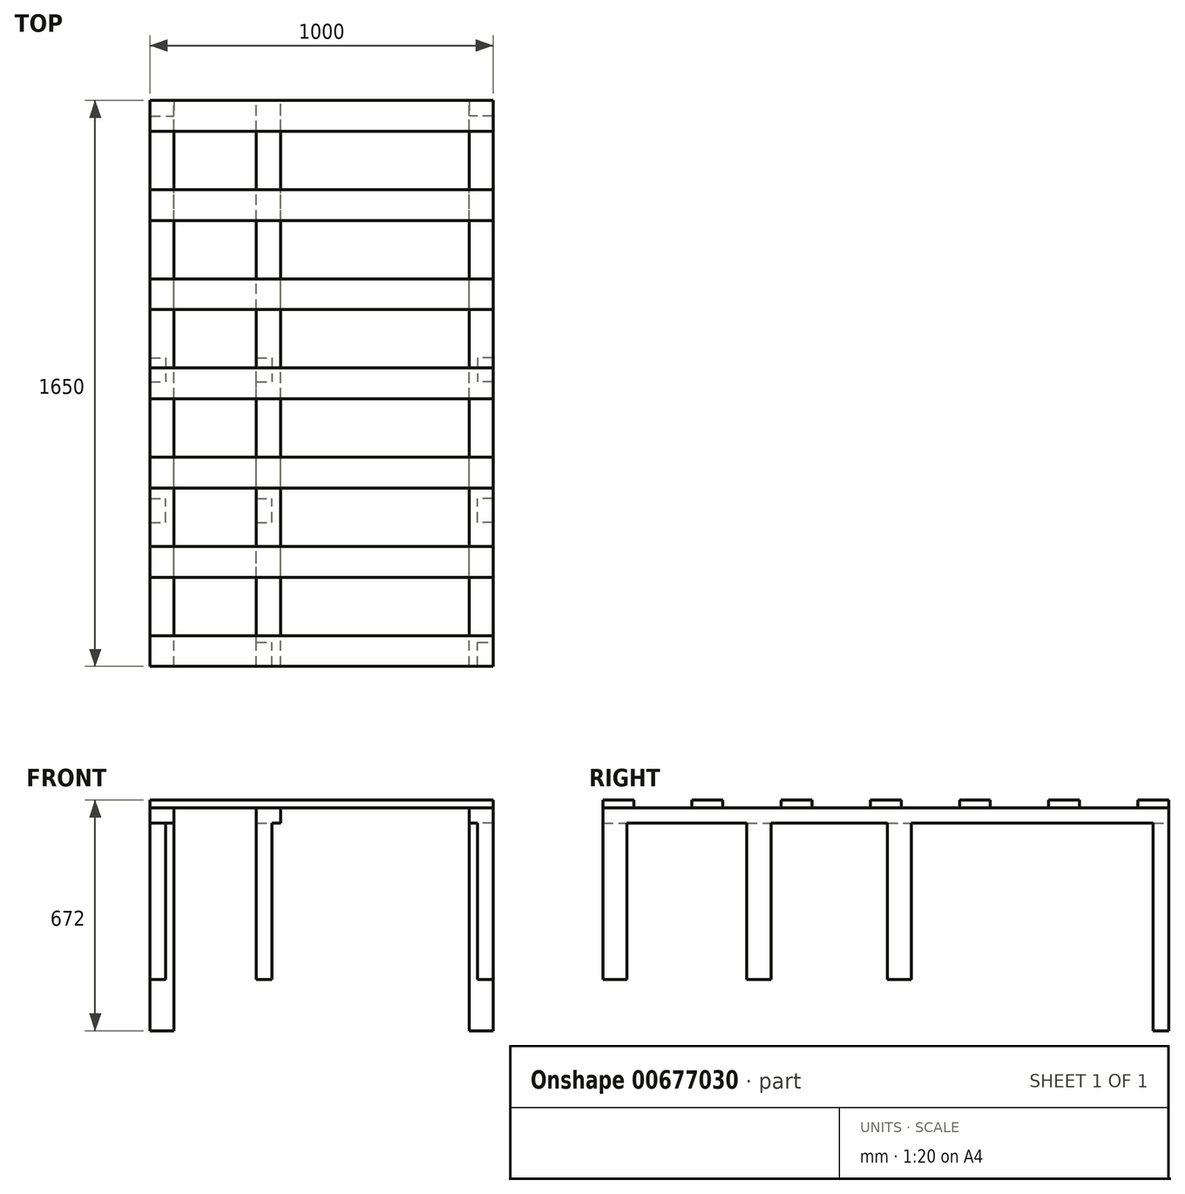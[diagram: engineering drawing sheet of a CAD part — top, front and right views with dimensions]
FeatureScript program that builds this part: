
annotation { "Feature Type Name" : "Feature", "Feature Type Description" : "" }
export const myFeature = defineFeature(function(context is Context, id is Id, definition is map)
    precondition{}
    {
        {
            var Q0;
            Q0=qCreatedBy(makeId("Top.planeOp"),FACE);
            var sketch = newSketch(context, id + "F0", { "sketchPlane" : qUnion([Q0])});
            skLineSegment(sketch, "E0.MirrorCS", {"start": v(-35, -1650) * mm, "end": v(35, -1650) * mm});
            skLineSegment(sketch, "E1.MirrorCS", {"start": v(-35, 0) * mm, "end": v(35, 0) * mm});
            skLineSegment(sketch, "E2.MirrorCS", {"start": v(655, 0) * mm, "end": v(585, 0) * mm});
            skLineSegment(sketch, "E3.MirrorCS", {"start": v(-345, 0) * mm, "end": v(-275, 0) * mm});
            skLineSegment(sketch, "E4.MirrorCS", {"start": v(-275, -1650) * mm, "end": v(-275, 0) * mm});
            skLineSegment(sketch, "E5.MirrorCS", {"start": v(585, -1650) * mm, "end": v(585, 0) * mm});
            skLineSegment(sketch, "E6.MirrorCS", {"start": v(35, -1650) * mm, "end": v(35, 0) * mm});
            skLineSegment(sketch, "E7.MirrorCS", {"start": v(655, -1650) * mm, "end": v(655, 0) * mm});
            skLineSegment(sketch, "E8.MirrorCS", {"start": v(-345, -1650) * mm, "end": v(-345, 0) * mm});
            skLineSegment(sketch, "E9.MirrorCS", {"start": v(-35, -1650) * mm, "end": v(-35, 0) * mm});
            skLineSegment(sketch, "E10.MirrorCS", {"start": v(0, -2563.12) * mm, "end": v(0, 0) * mm, "construction": true});
            skLineSegment(sketch, "E11", {"start": v(655, -1650) * mm, "end": v(585, -1650) * mm});
            skLineSegment(sketch, "E12", {"start": v(-275, -1650) * mm, "end": v(-345, -1650) * mm});
            skLineSegment(sketch, "E13", {"start": v(585, 0) * mm, "end": v(-345, 0) * mm, "construction": true});
            skLineSegment(sketch, "E14", {"start": v(585, -1650) * mm, "end": v(-275, -1650) * mm, "construction": true});
            skSolve(sketch);
        }
        {
            var Q0;
            Q0 = qSketchRegion(id + "F0", true);
            var Q1;
            {var subQ0=sQuery(id+"F0.wireOp",EDGE,"24e93d22-9b63-4a5b-b6a3-05b6ad89516c20.MirrorCS");var subQ1=sQuery(id+"F0.wireOp",EDGE,"E6.MirrorCS");var subQ2=makeQuery(id+"F0.imprint","INTERSECT",VERTEX,{"derivedFrom":[subQ1,subQ0]});Q1=makeQuery(id+"F0.imprint","IMPRINT",FACE,{"disambiguationData":[TD([[makeQuery(id+"F0.imprint","IMPRINT",EDGE,{"disambiguationData":[TD([[subQ2,-1.0]])],"derivedFrom":subQ1}),1.0]])]});}
            extrude(context, id + "F1", {"entities" : qUnion([Q0, Q1]), "depth" : 45 * mm, "offsetDistance" : 25 * mm});
        }
        {
            var Q0;
            Q0=makeQuery(id+"F1.opExtrude","CAP_FACE",FACE,{"disambiguationData":[OSD([sQuery(id+"F0.wireOp",EDGE,"E1.MirrorCS"),sQuery(id+"F0.wireOp",EDGE,"E2.MirrorCS"),sQuery(id+"F0.wireOp",EDGE,"E3.MirrorCS"),sQuery(id+"F0.wireOp",EDGE,"E4.MirrorCS"),sQuery(id+"F0.wireOp",EDGE,"E5.MirrorCS"),sQuery(id+"F0.wireOp",EDGE,"E6.MirrorCS"),sQuery(id+"F0.wireOp",EDGE,"24e93d22-9b63-4a5b-b6a3-05b6ad89516c14.MirrorCS"),sQuery(id+"F0.wireOp",EDGE,"E7.MirrorCS"),sQuery(id+"F0.wireOp",EDGE,"E8.MirrorCS"),sQuery(id+"F0.wireOp",EDGE,"E9.MirrorCS"),sQuery(id+"F0.wireOp",EDGE,"24e93d22-9b63-4a5b-b6a3-05b6ad89516c20.MirrorCS")])],"isStart":true});
            var sketch = newSketch(context, id + "F2", { "sketchPlane" : qUnion([Q0])});
            skLineSegment(sketch, "E15.bottom", {"start": v(610, 1650) * mm, "end": v(655, 1650) * mm});
            skLineSegment(sketch, "E15.top", {"start": v(610, 1580) * mm, "end": v(655, 1580) * mm});
            skLineSegment(sketch, "E15.left", {"start": v(610, 1650) * mm, "end": v(610, 1580) * mm});
            skLineSegment(sketch, "E15.right", {"start": v(655, 1650) * mm, "end": v(655, 1580) * mm});
            skLineSegment(sketch, "E16", {"start": v(-766.64, 750) * mm, "end": v(804.53, 750) * mm, "construction": true});
            skLineSegment(sketch, "E17.bottom", {"start": v(-345, 750) * mm, "end": v(-300, 750) * mm});
            skLineSegment(sketch, "E17.top", {"start": v(-345, 820) * mm, "end": v(-300, 820) * mm});
            skLineSegment(sketch, "E17.left", {"start": v(-345, 750) * mm, "end": v(-345, 820) * mm});
            skLineSegment(sketch, "E17.right", {"start": v(-300, 750) * mm, "end": v(-300, 820) * mm});
            skLineSegment(sketch, "E18.bottom", {"start": v(655, 750) * mm, "end": v(610, 750) * mm});
            skLineSegment(sketch, "E18.top", {"start": v(655, 820) * mm, "end": v(610, 820) * mm});
            skLineSegment(sketch, "E18.left", {"start": v(655, 750) * mm, "end": v(655, 820) * mm});
            skLineSegment(sketch, "E18.right", {"start": v(610, 750) * mm, "end": v(610, 820) * mm});
            skLineSegment(sketch, "E19.bottom", {"start": v(-345, 0) * mm, "end": v(-275, 0) * mm});
            skLineSegment(sketch, "E19.top", {"start": v(-345, 45) * mm, "end": v(-275, 45) * mm});
            skLineSegment(sketch, "E19.left", {"start": v(-345, 0) * mm, "end": v(-345, 45) * mm});
            skLineSegment(sketch, "E19.right", {"start": v(-275, 0) * mm, "end": v(-275, 45) * mm});
            skLineSegment(sketch, "E20.bottom", {"start": v(655, 0) * mm, "end": v(585, 0) * mm});
            skLineSegment(sketch, "E20.top", {"start": v(655, 45) * mm, "end": v(585, 45) * mm});
            skLineSegment(sketch, "E20.left", {"start": v(655, 0) * mm, "end": v(655, 45) * mm});
            skLineSegment(sketch, "E20.right", {"start": v(585, 0) * mm, "end": v(585, 45) * mm});
            skLineSegment(sketch, "E21.bottom", {"start": v(-35, 750) * mm, "end": v(10, 750) * mm});
            skLineSegment(sketch, "E21.top", {"start": v(-35, 820) * mm, "end": v(10, 820) * mm});
            skLineSegment(sketch, "E21.left", {"start": v(-35, 750) * mm, "end": v(-35, 820) * mm});
            skLineSegment(sketch, "E21.right", {"start": v(10, 750) * mm, "end": v(10, 820) * mm});
            skLineSegment(sketch, "E22.bottom", {"start": v(-345, 1650) * mm, "end": v(-300, 1650) * mm});
            skLineSegment(sketch, "E22.top", {"start": v(-345, 1580) * mm, "end": v(-300, 1580) * mm});
            skLineSegment(sketch, "E22.left", {"start": v(-345, 1650) * mm, "end": v(-345, 1580) * mm});
            skLineSegment(sketch, "E22.right", {"start": v(-300, 1650) * mm, "end": v(-300, 1580) * mm});
            skLineSegment(sketch, "E23.bottom", {"start": v(-35, 1650) * mm, "end": v(10, 1650) * mm});
            skLineSegment(sketch, "E23.top", {"start": v(-35, 1580) * mm, "end": v(10, 1580) * mm});
            skLineSegment(sketch, "E23.left", {"start": v(-35, 1650) * mm, "end": v(-35, 1580) * mm});
            skLineSegment(sketch, "E23.right", {"start": v(10, 1650) * mm, "end": v(10, 1580) * mm});
            skLineSegment(sketch, "E24.bottom", {"start": v(-345, 1230) * mm, "end": v(-300, 1230) * mm});
            skLineSegment(sketch, "E24.top", {"start": v(-345, 1160) * mm, "end": v(-300, 1160) * mm});
            skLineSegment(sketch, "E24.left", {"start": v(-345, 1230) * mm, "end": v(-345, 1160) * mm});
            skLineSegment(sketch, "E24.right", {"start": v(-300, 1230) * mm, "end": v(-300, 1160) * mm});
            skLineSegment(sketch, "E25.bottom", {"start": v(-35, 1230) * mm, "end": v(10, 1230) * mm});
            skLineSegment(sketch, "E25.top", {"start": v(-35, 1160) * mm, "end": v(10, 1160) * mm});
            skLineSegment(sketch, "E25.left", {"start": v(-35, 1230) * mm, "end": v(-35, 1160) * mm});
            skLineSegment(sketch, "E25.right", {"start": v(10, 1230) * mm, "end": v(10, 1160) * mm});
            skLineSegment(sketch, "E26.bottom", {"start": v(655, 1230) * mm, "end": v(610, 1230) * mm});
            skLineSegment(sketch, "E26.top", {"start": v(655, 1160) * mm, "end": v(610, 1160) * mm});
            skLineSegment(sketch, "E26.left", {"start": v(655, 1230) * mm, "end": v(655, 1160) * mm});
            skLineSegment(sketch, "E26.right", {"start": v(610, 1230) * mm, "end": v(610, 1160) * mm});
            skSolve(sketch);
        }
        {
            var Q0;
            Q0=makeQuery(id+"F2.imprint","IMPRINT",FACE,{"disambiguationData":[TD([[makeQuery(id+"F2.imprint","IMPRINT",EDGE,{"derivedFrom":sQuery(id+"F2.wireOp",EDGE,"5eMDLnCV-bmmW-PQH0-O9uX-ZlrQEPOtWy0S.bottom")}),-1.0]])]});
            var Q1;
            Q1=makeQuery(id+"F2.imprint","IMPRINT",FACE,{"disambiguationData":[TD([[makeQuery(id+"F2.imprint","IMPRINT",EDGE,{"derivedFrom":sQuery(id+"F2.wireOp",EDGE,"E15.bottom")}),-1.0]])]});
            var Q2;
            Q2=makeQuery(id+"F2.imprint","IMPRINT",FACE,{"disambiguationData":[TD([[makeQuery(id+"F2.imprint","IMPRINT",EDGE,{"derivedFrom":sQuery(id+"F2.wireOp",EDGE,"W4U25JQ1-nwdE-9fN8-cQUP-Vni1TVurAjkq.bottom")}),-1.0]])]});
            var Q3;
            Q3=makeQuery(id+"F2.imprint","IMPRINT",FACE,{"disambiguationData":[TD([[makeQuery(id+"F2.imprint","IMPRINT",EDGE,{"derivedFrom":sQuery(id+"F2.wireOp",EDGE,"VCQk6Hkw-atmi-mENE-ZOvr-ixRpdrlOzt6D.bottom")}),-1.0]])]});
            var Q4;
            Q4=makeQuery(id+"F2.imprint","IMPRINT",FACE,{"disambiguationData":[TD([[makeQuery(id+"F2.imprint","IMPRINT",EDGE,{"derivedFrom":sQuery(id+"F2.wireOp",EDGE,"945ca140-f328-402a-bb44-f249832b75310.MirrorCS")}),1.0]])]});
            var Q5;
            Q5=makeQuery(id+"F2.imprint","IMPRINT",FACE,{"disambiguationData":[TD([[makeQuery(id+"F2.imprint","IMPRINT",EDGE,{"derivedFrom":sQuery(id+"F2.wireOp",EDGE,"E18.bottom")}),-1.0]])]});
            var Q6;
            Q6=makeQuery(id+"F2.imprint","IMPRINT",FACE,{"disambiguationData":[TD([[makeQuery(id+"F2.imprint","IMPRINT",EDGE,{"derivedFrom":sQuery(id+"F2.wireOp",EDGE,"E17.bottom")}),1.0]])]});
            var Q7;
            Q7=makeQuery(id+"F2.imprint","IMPRINT",FACE,{"disambiguationData":[TD([[makeQuery(id+"F2.imprint","IMPRINT",EDGE,{"derivedFrom":sQuery(id+"F2.wireOp",EDGE,"E21.bottom")}),1.0]])]});
            var Q8;
            Q8=makeQuery(id+"F2.imprint","IMPRINT",FACE,{"disambiguationData":[TD([[makeQuery(id+"F2.imprint","IMPRINT",EDGE,{"derivedFrom":sQuery(id+"F2.wireOp",EDGE,"E22.bottom")}),1.0]])]});
            var Q9;
            Q9=makeQuery(id+"F2.imprint","IMPRINT",FACE,{"disambiguationData":[TD([[makeQuery(id+"F2.imprint","IMPRINT",EDGE,{"derivedFrom":sQuery(id+"F2.wireOp",EDGE,"E23.bottom")}),-1.0]])]});
            var Q10;
            Q10=makeQuery(id+"F2.imprint","IMPRINT",FACE,{"disambiguationData":[TD([[makeQuery(id+"F2.imprint","IMPRINT",EDGE,{"derivedFrom":sQuery(id+"F2.wireOp",EDGE,"E15.bottom")}),1.0]])]});
            var Q11;
            Q11=makeQuery(id+"F2.imprint","IMPRINT",FACE,{"disambiguationData":[TD([[makeQuery(id+"F2.imprint","IMPRINT",EDGE,{"derivedFrom":sQuery(id+"F2.wireOp",EDGE,"E24.bottom")}),-1.0]])]});
            var Q12;
            Q12=makeQuery(id+"F2.imprint","IMPRINT",FACE,{"disambiguationData":[TD([[makeQuery(id+"F2.imprint","IMPRINT",EDGE,{"derivedFrom":sQuery(id+"F2.wireOp",EDGE,"E25.bottom")}),-1.0]])]});
            var Q13;
            Q13=makeQuery(id+"F2.imprint","IMPRINT",FACE,{"disambiguationData":[TD([[makeQuery(id+"F2.imprint","IMPRINT",EDGE,{"derivedFrom":sQuery(id+"F2.wireOp",EDGE,"E26.bottom")}),1.0]])]});
            extrude(context, id + "F3", {"entities" : qUnion([Q0, Q1, Q2, Q3, Q4, Q5, Q6, Q7, Q8, Q9, Q10, Q11, Q12, Q13]), "operationType" : NewBodyOperationType.ADD, "depth" : 455 * mm, "offsetDistance" : 25 * mm});
        }
        {
            var Q0;
            Q0=makeQuery(id+"F2.imprint","IMPRINT",FACE,{"disambiguationData":[TD([[makeQuery(id+"F2.imprint","IMPRINT",EDGE,{"derivedFrom":sQuery(id+"F2.wireOp",EDGE,"E20.bottom")}),1.0]])]});
            var Q1;
            Q1=makeQuery(id+"F2.imprint","IMPRINT",FACE,{"disambiguationData":[TD([[makeQuery(id+"F2.imprint","IMPRINT",EDGE,{"derivedFrom":sQuery(id+"F2.wireOp",EDGE,"E20.bottom")}),-1.0]])]});
            var Q2;
            Q2=makeQuery(id+"F2.imprint","IMPRINT",FACE,{"disambiguationData":[TD([[makeQuery(id+"F2.imprint","IMPRINT",EDGE,{"derivedFrom":sQuery(id+"F2.wireOp",EDGE,"E19.bottom")}),1.0]])]});
            extrude(context, id + "F4", {"entities" : qUnion([Q0, Q1, Q2]), "operationType" : NewBodyOperationType.ADD, "depth" : 605 * mm, "offsetDistance" : 25 * mm});
        }
        {
            var Q0;
            Q0=makeQuery(id+"F1.opExtrude","CAP_FACE",FACE,{"disambiguationData":[OSD([sQuery(id+"F0.wireOp",EDGE,"E3.MirrorCS"),sQuery(id+"F0.wireOp",EDGE,"E4.MirrorCS"),sQuery(id+"F0.wireOp",EDGE,"E8.MirrorCS"),sQuery(id+"F0.wireOp",EDGE,"E12")])],"isStart":false});
            var sketch = newSketch(context, id + "F5", { "sketchPlane" : qUnion([Q0])});
            skLineSegment(sketch, "E27.bottom", {"start": v(-345, -1650) * mm, "end": v(655, -1650) * mm});
            skLineSegment(sketch, "E27.top", {"start": v(-345, -1560) * mm, "end": v(655, -1560) * mm});
            skLineSegment(sketch, "E27.left", {"start": v(-345, -1650) * mm, "end": v(-345, -1560) * mm});
            skLineSegment(sketch, "E27.right", {"start": v(655, -1650) * mm, "end": v(655, -1560) * mm});
            skLineSegment(sketch, "E28.bottom", {"start": v(-345, 0) * mm, "end": v(655, 0) * mm});
            skLineSegment(sketch, "E28.top", {"start": v(-345, -90) * mm, "end": v(655, -90) * mm});
            skLineSegment(sketch, "E28.left", {"start": v(-345, 0) * mm, "end": v(-345, -90) * mm});
            skLineSegment(sketch, "E28.right", {"start": v(655, 0) * mm, "end": v(655, -90) * mm});
            skLineSegment(sketch, "E29.bottom", {"start": v(-345, -260) * mm, "end": v(655, -260) * mm});
            skLineSegment(sketch, "E29.top", {"start": v(-345, -350) * mm, "end": v(655, -350) * mm});
            skLineSegment(sketch, "E29.left", {"start": v(-345, -260) * mm, "end": v(-345, -350) * mm});
            skLineSegment(sketch, "E29.right", {"start": v(655, -260) * mm, "end": v(655, -350) * mm});
            skLineSegment(sketch, "E30.bottom", {"start": v(-345, -520) * mm, "end": v(655, -520) * mm});
            skLineSegment(sketch, "E30.top", {"start": v(-345, -610) * mm, "end": v(655, -610) * mm});
            skLineSegment(sketch, "E30.left", {"start": v(-345, -520) * mm, "end": v(-345, -610) * mm});
            skLineSegment(sketch, "E30.right", {"start": v(655, -520) * mm, "end": v(655, -610) * mm});
            skLineSegment(sketch, "E31.bottom", {"start": v(-345, -780) * mm, "end": v(655, -780) * mm});
            skLineSegment(sketch, "E31.top", {"start": v(-345, -870) * mm, "end": v(655, -870) * mm});
            skLineSegment(sketch, "E31.left", {"start": v(-345, -780) * mm, "end": v(-345, -870) * mm});
            skLineSegment(sketch, "E31.right", {"start": v(655, -780) * mm, "end": v(655, -870) * mm});
            skLineSegment(sketch, "E32.bottom", {"start": v(-345, -1040) * mm, "end": v(655, -1040) * mm});
            skLineSegment(sketch, "E32.top", {"start": v(-345, -1130) * mm, "end": v(655, -1130) * mm});
            skLineSegment(sketch, "E32.left", {"start": v(-345, -1040) * mm, "end": v(-345, -1130) * mm});
            skLineSegment(sketch, "E32.right", {"start": v(655, -1040) * mm, "end": v(655, -1130) * mm});
            skLineSegment(sketch, "E33.bottom", {"start": v(-345, -1300) * mm, "end": v(655, -1300) * mm});
            skLineSegment(sketch, "E33.top", {"start": v(-345, -1390) * mm, "end": v(655, -1390) * mm});
            skLineSegment(sketch, "E33.left", {"start": v(-345, -1300) * mm, "end": v(-345, -1390) * mm});
            skLineSegment(sketch, "E33.right", {"start": v(655, -1300) * mm, "end": v(655, -1390) * mm});
            skSolve(sketch);
        }
        {
            var Q0;
            {var subQ3=sQuery(id+"F5.wireOp",EDGE,"E27.left");Q0=makeQuery(id+"F5.imprint","IMPRINT",FACE,{"disambiguationData":[TD([[makeQuery(id+"F5.imprint","IMPRINT",EDGE,{"derivedFrom":subQ3}),-1.0]])]});}
            var Q1;
            {var subQ3=sQuery(id+"F5.wireOp",EDGE,"E27.right");Q1=makeQuery(id+"F5.imprint","IMPRINT",FACE,{"disambiguationData":[TD([[makeQuery(id+"F5.imprint","IMPRINT",EDGE,{"derivedFrom":subQ3}),1.0]])]});}
            var Q2;
            {var subQ0=sQuery(id+"F5.wireOp",EDGE,"E33.left");Q2=makeQuery(id+"F5.imprint","IMPRINT",FACE,{"disambiguationData":[TD([[makeQuery(id+"F5.imprint","IMPRINT",EDGE,{"derivedFrom":subQ0}),-1.0]])]});}
            var Q3;
            {var subQ0=sQuery(id+"F5.wireOp",EDGE,"E33.right");Q3=makeQuery(id+"F5.imprint","IMPRINT",FACE,{"disambiguationData":[TD([[makeQuery(id+"F5.imprint","IMPRINT",EDGE,{"derivedFrom":subQ0}),-1.0]])]});}
            var Q4;
            {var subQ0=sQuery(id+"F5.wireOp",EDGE,"E32.left");Q4=makeQuery(id+"F5.imprint","IMPRINT",FACE,{"disambiguationData":[TD([[makeQuery(id+"F5.imprint","IMPRINT",EDGE,{"derivedFrom":subQ0}),-1.0]])]});}
            var Q5;
            {var subQ0=sQuery(id+"F5.wireOp",EDGE,"E32.right");Q5=makeQuery(id+"F5.imprint","IMPRINT",FACE,{"disambiguationData":[TD([[makeQuery(id+"F5.imprint","IMPRINT",EDGE,{"derivedFrom":subQ0}),-1.0]])]});}
            var Q6;
            {var subQ0=sQuery(id+"F5.wireOp",EDGE,"E31.left");Q6=makeQuery(id+"F5.imprint","IMPRINT",FACE,{"disambiguationData":[TD([[makeQuery(id+"F5.imprint","IMPRINT",EDGE,{"derivedFrom":subQ0}),-1.0]])]});}
            var Q7;
            {var subQ0=sQuery(id+"F5.wireOp",EDGE,"E31.right");Q7=makeQuery(id+"F5.imprint","IMPRINT",FACE,{"disambiguationData":[TD([[makeQuery(id+"F5.imprint","IMPRINT",EDGE,{"derivedFrom":subQ0}),-1.0]])]});}
            var Q8;
            {var subQ0=sQuery(id+"F5.wireOp",EDGE,"E30.left");Q8=makeQuery(id+"F5.imprint","IMPRINT",FACE,{"disambiguationData":[TD([[makeQuery(id+"F5.imprint","IMPRINT",EDGE,{"derivedFrom":subQ0}),-1.0]])]});}
            var Q9;
            {var subQ0=sQuery(id+"F5.wireOp",EDGE,"E30.right");Q9=makeQuery(id+"F5.imprint","IMPRINT",FACE,{"disambiguationData":[TD([[makeQuery(id+"F5.imprint","IMPRINT",EDGE,{"derivedFrom":subQ0}),-1.0]])]});}
            var Q10;
            {var subQ0=sQuery(id+"F5.wireOp",EDGE,"E29.left");Q10=makeQuery(id+"F5.imprint","IMPRINT",FACE,{"disambiguationData":[TD([[makeQuery(id+"F5.imprint","IMPRINT",EDGE,{"derivedFrom":subQ0}),-1.0]])]});}
            var Q11;
            {var subQ0=sQuery(id+"F5.wireOp",EDGE,"E29.right");Q11=makeQuery(id+"F5.imprint","IMPRINT",FACE,{"disambiguationData":[TD([[makeQuery(id+"F5.imprint","IMPRINT",EDGE,{"derivedFrom":subQ0}),-1.0]])]});}
            var Q12;
            {var subQ0=sQuery(id+"F5.wireOp",EDGE,"E28.left");Q12=makeQuery(id+"F5.imprint","IMPRINT",FACE,{"disambiguationData":[TD([[makeQuery(id+"F5.imprint","IMPRINT",EDGE,{"derivedFrom":subQ0}),-1.0]])]});}
            var Q13;
            {var subQ3=sQuery(id+"F5.wireOp",EDGE,"E28.right");Q13=makeQuery(id+"F5.imprint","IMPRINT",FACE,{"disambiguationData":[TD([[makeQuery(id+"F5.imprint","IMPRINT",EDGE,{"derivedFrom":subQ3}),-1.0]])]});}
            extrude(context, id + "F6", {"entities" : qUnion([Q0, Q1, Q2, Q3, Q4, Q5, Q6, Q7, Q8, Q9, Q10, Q11, Q12, Q13]), "depth" : 22 * mm, "offsetDistance" : 25 * mm});
        }
    });
